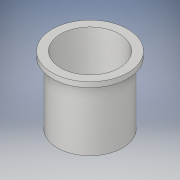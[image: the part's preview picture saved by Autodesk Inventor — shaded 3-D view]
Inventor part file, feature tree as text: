
AUTODESK INVENTOR PART (.ipt)
format: ipt  version: 2017 (Build 210142000, 142)  size: 166,912 bytes
history: native  units: in
note: dims shown in document units (in); Inventor stores cm internally (conversion verified against a paired STEP export)
features: revolve x1, sketch x1
ambient origin geometry x8: Origin, YZ Plane, XZ Plane, XY Plane, X Axis, Y Axis, Z Axis, Center Point
bodies: Solid1 (feature_tree)
feature tree (2):
  revolve  "Revolution1"  [1 undecoded]
  sketch  "Sketch1"  dims[d0=1.13in d1=3.7in d2=0.125in d3=0.1718in d5=1.0in d6=1.0in d7=90.0deg d8=0.5in d9=15.0deg d12=1.25in d13=0.25in d16=0.5in d17=0.5in d18=0.5in d19=2.5in d20=0.5in d22=0.375in d23=0.25in d25=0.234in d26=15.0deg d27=0.125in d28=0.25in d29=1.0in d30=4.25in d31=0.25in d32=1.0in d33=90.0deg]
note: 1 required parameter value undecoded (feature->parameter linkage not recoverable at this tier; creation-order binding heuristic only, values carry confidence <= 0.55)
